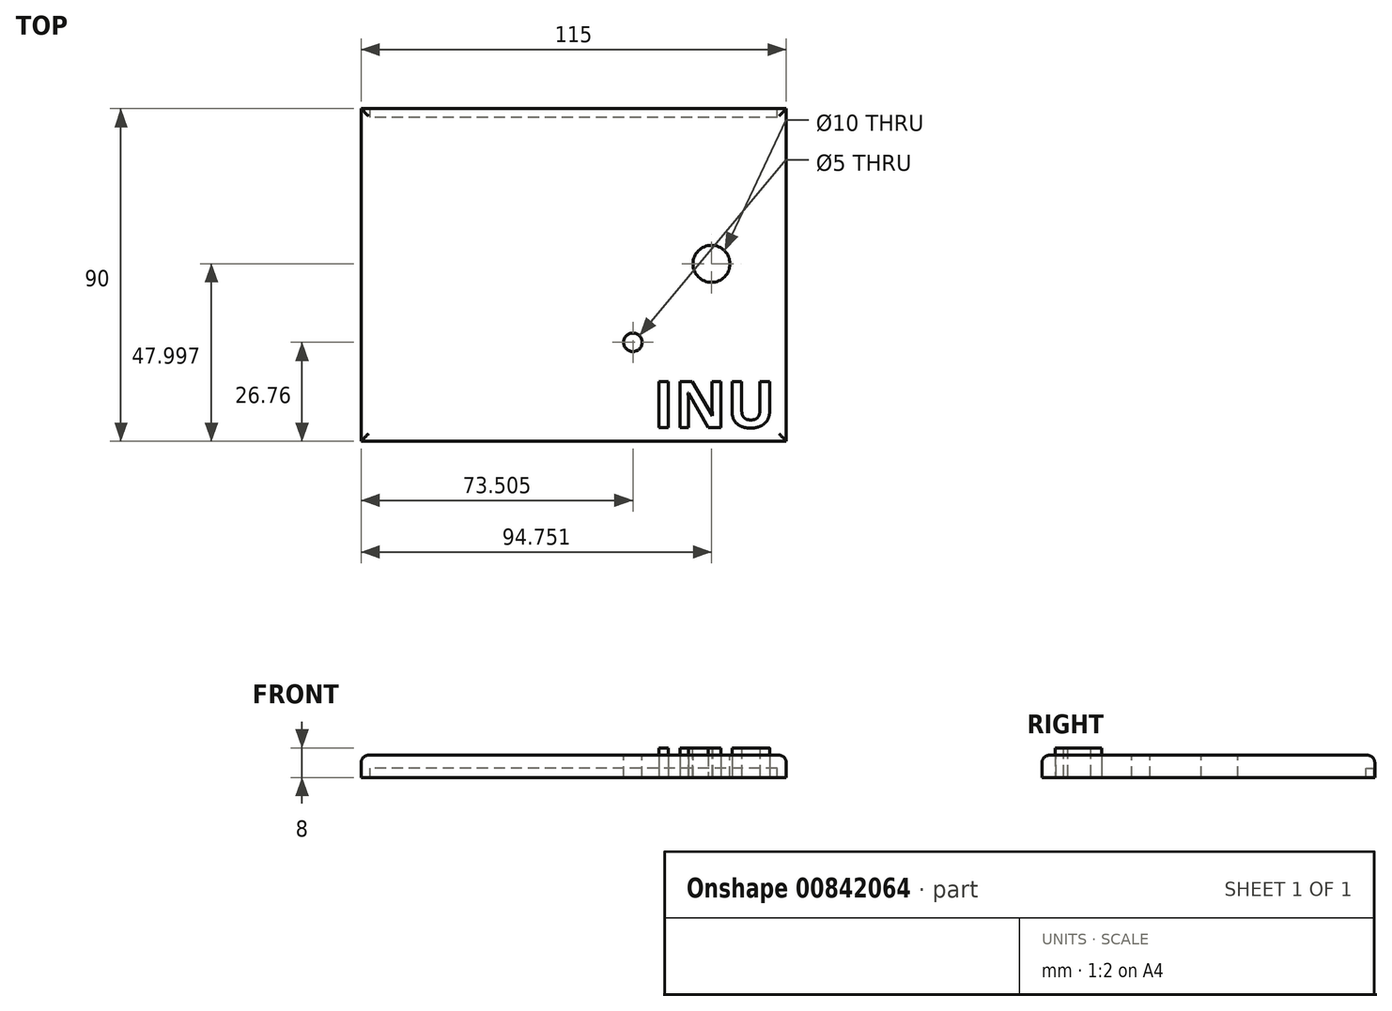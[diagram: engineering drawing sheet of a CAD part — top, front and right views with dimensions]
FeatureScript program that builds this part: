
annotation { "Feature Type Name" : "Feature", "Feature Type Description" : "" }
export const myFeature = defineFeature(function(context is Context, id is Id, definition is map)
    precondition{}
    {
        {
            var Q0;
            Q0=qCreatedBy(makeId("Top.planeOp"),FACE);
            var sketch = newSketch(context, id + "F0", { "sketchPlane" : qUnion([Q0])});
            skLineSegment(sketch, "E0.bottom", {"start": v(-57.5, 38.17) * mm, "end": v(57.5, 38.17) * mm});
            skLineSegment(sketch, "E0.top", {"start": v(-57.5, -51.83) * mm, "end": v(57.5, -51.83) * mm});
            skLineSegment(sketch, "E0.left", {"start": v(-57.5, 38.17) * mm, "end": v(-57.5, -51.83) * mm});
            skLineSegment(sketch, "E0.right", {"start": v(57.5, 38.17) * mm, "end": v(57.5, -51.83) * mm});
            skLineSegment(sketch, "E1", {"start": v(0, -33.4) * mm, "end": v(57.5, -33.4) * mm});
            skSolve(sketch);
        }
        {
            var Q0;
            Q0=makeQuery(id+"F0.imprint","IMPRINT",FACE,{"disambiguationData":[TD([[makeQuery(id+"F0.imprint","IMPRINT",EDGE,{"derivedFrom":sQuery(id+"F0.wireOp",EDGE,"E0.bottom")}),-1.0]])]});
            extrude(context, id + "F1", {"entities" : qUnion([Q0]), "depth" : 6 * mm, "offsetDistance" : 25 * mm});
        }
        {
            var Q0;
            Q0=makeQuery(id+"F0.imprint","IMPRINT",FACE,{"disambiguationData":[TD([[makeQuery(id+"F0.imprint","IMPRINT",EDGE,{"derivedFrom":sQuery(id+"F0.wireOp",EDGE,"E0.bottom")}),-1.0]])]});
            var sketch = newSketch(context, id + "F2", { "sketchPlane" : qUnion([Q0])});
            skText(sketch, "E2", { "text": "INU", "fontName": "OpenSans-Bold.ttf"});
            const initialGuessF2  = {"E2": [0.02142, -0.04812, 1, 0, 0.01252]};
            skSetInitialGuess(sketch, initialGuessF2);
            skSolve(sketch);
        }
        {
            var Q0;
            Q0 = qSketchRegion(id + "F2", true);
            var Q1;
            Q1=sQuery(id+"F2.wireOp",EDGE,"IfVCwf1X-MvmI-579h-j2cM-j51mp9BmZJXM");
            var Q2;
            Q2=sQuery(id+"F2.wireOp",EDGE,"8Dj4XB12-rUho-raSa-ERVi-O2vDwdI9fXqb");
            var Q3;
            Q3=sQuery(id+"F2.wireOp",EDGE,"NHptyHmu-lKRW-OREP-nzQm-42sDeTICPHU1");
            var Q4;
            Q4=sQuery(id+"F2.wireOp",EDGE,"iTowa3bQ-PUtq-0wbT-se3f-CsOyaGs1xgYn");
            var Q5;
            Q5=sQuery(id+"F2.wireOp",EDGE,"wLw318s5-R9BV-jXUg-VQic-UZRrx3XaGqgK");
            var Q6;
            Q6=sQuery(id+"F2.wireOp",EDGE,"nv8XZjOS-ZMdX-S9NX-hgss-oBTBxtV2lYex");
            var Q7;
            Q7=sQuery(id+"F2.wireOp",EDGE,"wyRAwZ5a-KhMs-gbjs-ZlDY-pe1N5wFFhKCc");
            var Q8;
            Q8=sQuery(id+"F2.wireOp",EDGE,"ncGyVwiV-LBzg-QzmT-VO2i-lYovLymnedsb");
            var Q9;
            Q9=sQuery(id+"F2.wireOp",EDGE,"D1uV4BMv-uXex-erl9-WFoX-RR9KzKwJF5iO");
            var Q10;
            Q10=sQuery(id+"F2.wireOp",EDGE,"jNtJ4Y08-Adu2-bPCR-iEcR-eq3JgoCI4CQY");
            var Q11;
            Q11=sQuery(id+"F2.wireOp",EDGE,"MP7CqESM-aYy0-ARWL-YNGI-RBZIkwnjcJcx");
            var Q12;
            Q12=sQuery(id+"F2.wireOp",EDGE,"lBivvepv-xFKJ-Frbz-HT2q-qLrLy82ywYHS");
            var Q13;
            Q13=sQuery(id+"F2.wireOp",EDGE,"mou0NU9w-6leY-Bz56-RQlX-FG7xUNE5uFQa");
            var Q14;
            Q14=sQuery(id+"F2.wireOp",EDGE,"ACfudDjN-kwdP-3v6F-zQtZ-lXS2iCcqi547");
            var Q15;
            Q15=sQuery(id+"F2.wireOp",EDGE,"zIcCQHSU-yq32-RFVt-5Vb9-EvsxOXage6Ex");
            var Q16;
            Q16=sQuery(id+"F2.wireOp",EDGE,"qlNpm7Jk-fsOX-uKVd-OHpz-fIvoERs7KCsr");
            var Q17;
            Q17=sQuery(id+"F2.wireOp",EDGE,"hGqVk0hf-Eazj-8S22-ivHf-iwlvqOFwFNkx");
            var Q18;
            Q18=sQuery(id+"F2.wireOp",EDGE,"4uZ4gqfQ-uAWZ-DGfh-ooDo-QNW0BhfoJ74f");
            var Q19;
            Q19=sQuery(id+"F2.wireOp",EDGE,"UFtROkqr-eqyM-crPf-ZsQk-adbbWBm5xOho");
            var Q20;
            Q20=sQuery(id+"F2.wireOp",EDGE,"hWSHyy29-5tNg-H2cV-hTLW-wt6VsTouW4oC");
            var Q21;
            Q21=sQuery(id+"F2.wireOp",EDGE,"PdI37mi9-DrOZ-H2eC-CVVr-nAfzsiUEKhxT");
            var Q22;
            Q22=sQuery(id+"F2.wireOp",EDGE,"ZQvtDhB2-iwT7-QUVj-fyxh-VIaVeeQzOlNC");
            var Q23;
            Q23=sQuery(id+"F2.wireOp",EDGE,"cRpZDD7R-j0hp-xZL8-dIGH-otkIcSfTwIDo");
            var Q24;
            Q24=sQuery(id+"F2.wireOp",EDGE,"RsubttPP-zQJ6-Bs4A-VxI7-r51VozqztY94");
            var Q25;
            Q25=sQuery(id+"F2.wireOp",EDGE,"ns4h3tx0-4iIg-GhaM-rlod-J7caOnPRk756");
            var Q26;
            Q26=sQuery(id+"F2.wireOp",EDGE,"E96szFua-Qb70-xTmp-WEW8-YHhT01Y6Tvof");
            var Q27;
            Q27=sQuery(id+"F2.wireOp",EDGE,"vAcTR4ZO-qIE8-ZpHg-CKLu-Ceah9BaVzeUD");
            var Q28;
            Q28=sQuery(id+"F2.wireOp",EDGE,"aXGO4l2R-9Zjp-7Fbz-FEpU-HhQd08GgCNJ8");
            var Q29;
            Q29=sQuery(id+"F2.wireOp",EDGE,"PWbTkrI6-TIXM-IZsS-0BrN-Ck1LI5G1gw9J");
            var Q30;
            Q30=sQuery(id+"F2.wireOp",EDGE,"fujB03zx-OvhH-bmMq-DLxv-PGjIpBh39Qf0");
            extrude(context, id + "F3", {"entities" : qUnion([Q0]), "surfaceEntities" : qUnion([Q1, Q2, Q3, Q4, Q5, Q6, Q7, Q8, Q9, Q10, Q11, Q12, Q13, Q14, Q15, Q16, Q17, Q18, Q19, Q20, Q21, Q22, Q23, Q24, Q25, Q26, Q27, Q28, Q29, Q30]), "depth" : 8 * mm, "offsetDistance" : 25 * mm});
        }
        {
            var Q0;
            Q0=makeQuery(id+"F1.opExtrude","CAP_FACE",FACE,{"disambiguationData":[OSD([sQuery(id+"F0.wireOp",EDGE,"E0.bottom"),sQuery(id+"F0.wireOp",EDGE,"E0.top"),sQuery(id+"F0.wireOp",EDGE,"E0.left"),sQuery(id+"F0.wireOp",EDGE,"E0.right")])],"isStart":false});
            fillet(context, id + "F4", {"entities" : qUnion([Q0]), "radius" : 2 * mm, "tangentPropagation" : true, "allowEdgeOverflow" : false});
        }
        {
            var Q0;
            Q0=makeQuery(id+"F1.opExtrude","CAP_FACE",FACE,{"disambiguationData":[OSD([sQuery(id+"F0.wireOp",EDGE,"E0.bottom"),sQuery(id+"F0.wireOp",EDGE,"E0.top"),sQuery(id+"F0.wireOp",EDGE,"E0.left"),sQuery(id+"F0.wireOp",EDGE,"E0.right")])],"isStart":false});
            var sketch = newSketch(context, id + "F5", { "sketchPlane" : qUnion([Q0])});
            skCircle(sketch, "E3", {"center": v(37.25, -3.83) * mm, "radius": 5 * mm});
            skLineSegment(sketch, "E4", {"start": v(55.25, -3.83) * mm, "end": v(37.25, -3.83) * mm});
            skLineSegment(sketch, "E5", {"start": v(37.25, -3.83) * mm, "end": v(37.25, 36.17) * mm});
            skCircle(sketch, "E6", {"center": v(16, -25.07) * mm, "radius": 2.5 * mm});
            skSolve(sketch);
        }
        {
            var Q0;
            Q0 = qSketchRegion(id + "F5", true);
            extrude(context, id + "F6", {"entities" : qUnion([Q0]), "operationType" : NewBodyOperationType.REMOVE, "oppositeDirection" : true, "depth" : 10 * mm, "offsetDistance" : 25 * mm});
        }
        {
            var Q0;
            Q0=qCreatedBy(makeId("Right.planeOp"),FACE);
            var sketch = newSketch(context, id + "F7", { "sketchPlane" : qUnion([Q0])});
            skLineSegment(sketch, "E7", {"start": v(37.9, 0) * mm, "end": v(38.1, 0) * mm});
            skLineSegment(sketch, "E8.bottom", {"start": v(35.8, 0) * mm, "end": v(37.9, 0) * mm});
            skLineSegment(sketch, "E8.top", {"start": v(35.8, 2.5) * mm, "end": v(37.9, 2.5) * mm});
            skLineSegment(sketch, "E8.left", {"start": v(35.8, 0) * mm, "end": v(35.8, 2.5) * mm});
            skLineSegment(sketch, "E8.right", {"start": v(37.9, 0) * mm, "end": v(37.9, 2.5) * mm});
            skSolve(sketch);
        }
        {
            var Q0;
            Q0 = qSketchRegion(id + "F7", true);
            extrude(context, id + "F8", {"entities" : qUnion([Q0]), "operationType" : NewBodyOperationType.REMOVE, "depth" : 110 * mm, "offsetDistance" : 25 * mm, "symmetric" : true});
        }
    });
